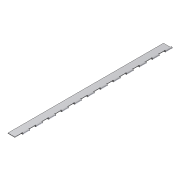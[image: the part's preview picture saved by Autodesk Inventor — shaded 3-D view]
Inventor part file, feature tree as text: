
AUTODESK INVENTOR PART (.ipt)
format: ipt  version: unknown  size: 225,280 bytes
history: native  units: in
note: dims shown in document units (in); Inventor stores cm internally (conversion verified against a paired STEP export)
features: extrude x2, sketch x2, pattern_linear x1
ambient origin geometry x8: Origin, YZ Plane, XZ Plane, XY Plane, X Axis, Y Axis, Z Axis, Center Point
bodies: Solid1 (feature_tree)
feature tree (5):
  extrude  "Extrusion1"  Depth=0.5in
  extrude  "Extrusion2"  Depth=2.5in
  pattern_linear  "Rectangular Pattern1"  Spacing1=48.0in  [1 undecoded]
  sketch  "Sketch1"  dims[d0=0.25in d1=0.5in]
  sketch  "Sketch2"  dims[d2=0.125in d3=2.5in d4=48.0in d5=0.0in d6=2.0in d7=0.625in d8=48.0in d9=0.0in d10=9.4488in d12=4.0in]
note: 1 required parameter value undecoded (feature->parameter linkage not recoverable at this tier; creation-order binding heuristic only, values carry confidence <= 0.55)
